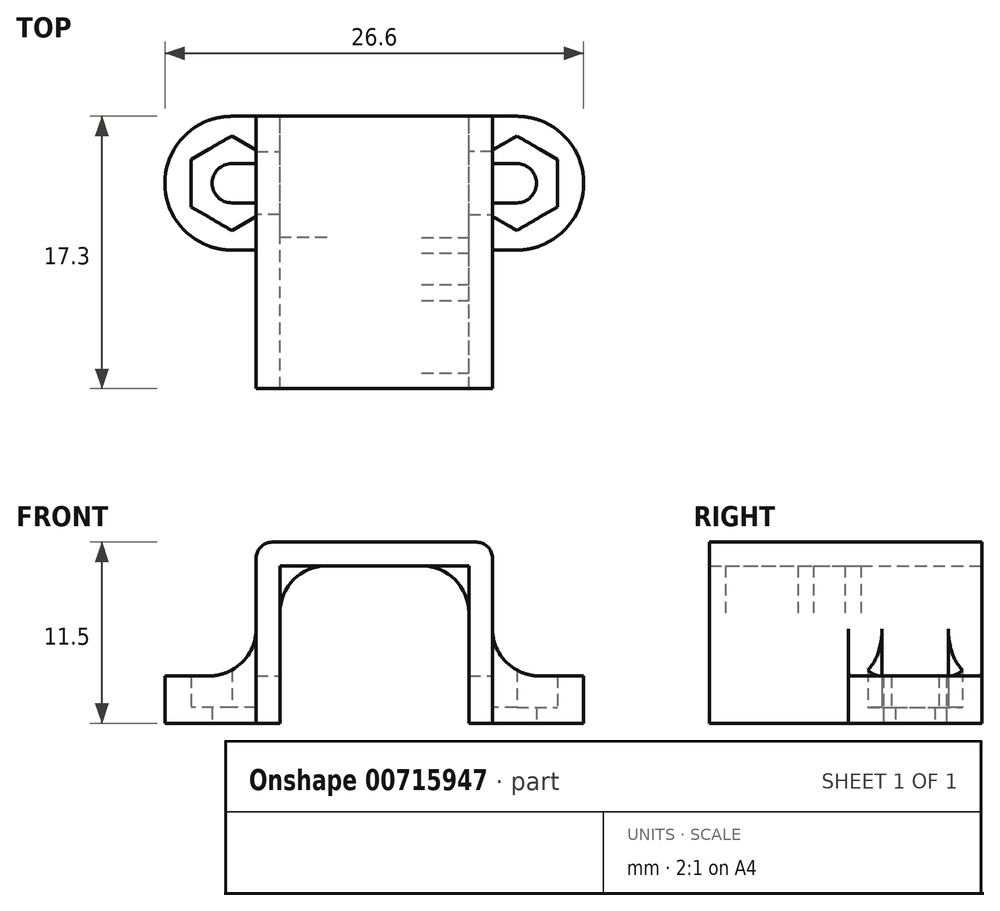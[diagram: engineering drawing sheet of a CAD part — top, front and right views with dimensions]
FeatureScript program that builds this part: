
annotation { "Feature Type Name" : "Feature", "Feature Type Description" : "" }
export const myFeature = defineFeature(function(context is Context, id is Id, definition is map)
    precondition{}
    {
        {
            var Q0;
            Q0=qCreatedBy(makeId("Front.planeOp"),FACE);
            var sketch = newSketch(context, id + "F0", { "sketchPlane" : qUnion([Q0])});
            skLineSegment(sketch, "E0", {"start": v(0, 11.5) * mm, "end": v(-6.5, 11.5) * mm});
            skLineSegment(sketch, "E1", {"start": v(-7.5, 10.5) * mm, "end": v(-7.5, 6) * mm});
            skLineSegment(sketch, "E2", {"start": v(-10.5, 3) * mm, "end": v(-13.3, 3) * mm});
            skLineSegment(sketch, "E3", {"start": v(-13.3, 3) * mm, "end": v(-13.3, 0) * mm});
            skLineSegment(sketch, "E4", {"start": v(-13.3, 0) * mm, "end": v(-6, 0) * mm});
            skLineSegment(sketch, "E5", {"start": v(-6, 0) * mm, "end": v(-6, 7) * mm});
            skLineSegment(sketch, "E6", {"start": v(-3, 10) * mm, "end": v(0, 10) * mm});
            skPoint(sketch, "E7.visualSharp", {"position": v(-7.5, 11.5) * mm});
            skArc(sketch, "E7.filletArc", {"start": v(-6.5, 11.5) * mm, "mid": v(-7.2, 11.2) * mm, "end": v(-7.5, 10.5) * mm});
            skPoint(sketch, "E8.visualSharp", {"position": v(-6, 10) * mm});
            skArc(sketch, "E8.filletArc", {"start": v(-3, 10) * mm, "mid": v(-5.12, 9.12) * mm, "end": v(-6, 7) * mm});
            skPoint(sketch, "E9.visualSharp", {"position": v(-7.5, 3) * mm});
            skArc(sketch, "E9.filletArc", {"start": v(-10.5, 3) * mm, "mid": v(-8.38, 3.88) * mm, "end": v(-7.5, 6) * mm});
            skLineSegment(sketch, "E10.MirrorCS", {"start": v(3, 10) * mm, "end": v(0, 10) * mm});
            skLineSegment(sketch, "E11.MirrorCS", {"start": v(0, 11.5) * mm, "end": v(6.5, 11.5) * mm});
            skArc(sketch, "E12.MirrorCS", {"start": v(3, 10) * mm, "mid": v(5.12, 9.12) * mm, "end": v(6, 7) * mm});
            skArc(sketch, "E13.MirrorCS", {"start": v(6.5, 11.5) * mm, "mid": v(7.2, 11.2) * mm, "end": v(7.5, 10.5) * mm});
            skLineSegment(sketch, "E14.MirrorCS", {"start": v(7.5, 10.5) * mm, "end": v(7.5, 6) * mm});
            skLineSegment(sketch, "E15.MirrorCS", {"start": v(6, 0) * mm, "end": v(6, 7) * mm});
            skArc(sketch, "E16.MirrorCS", {"start": v(10.5, 3) * mm, "mid": v(8.38, 3.88) * mm, "end": v(7.5, 6) * mm});
            skLineSegment(sketch, "E17.MirrorCS", {"start": v(10.5, 3) * mm, "end": v(13.3, 3) * mm});
            skLineSegment(sketch, "E18.MirrorCS", {"start": v(13.3, 3) * mm, "end": v(13.3, 0) * mm});
            skLineSegment(sketch, "E19.MirrorCS", {"start": v(13.3, 0) * mm, "end": v(6, 0) * mm});
            skSolve(sketch);
        }
        {
            var Q0;
            Q0=qSketchRegion(id+"F0",true);
            extrude(context, id + "F1", {"entities" : qUnion([Q0]), "depth" : 17.3 * mm});
        }
        {
            var Q0;
            Q0=makeQuery(id+"F1.opExtrude","SWEPT_FACE",FACE,{"disambiguationData":[OSD([sQuery(id+"F0.wireOp",EDGE,"E0"),sQuery(id+"F0.wireOp",EDGE,"E11.MirrorCS")])]});
            var sketch = newSketch(context, id + "F2", { "sketchPlane" : qUnion([Q0])});
            skLineSegment(sketch, "E20.2", {"start": v(-6.5, 0) * mm, "end": v(-7.5, 0) * mm});
            skLineSegment(sketch, "E20.3", {"start": v(-6.5, 0) * mm, "end": v(6.5, 0) * mm});
            skLineSegment(sketch, "E20.4", {"start": v(6.5, 0) * mm, "end": v(7.5, 0) * mm});
            skLineSegment(sketch, "E20.7", {"start": v(6.5, -17.3) * mm, "end": v(7.5, -17.3) * mm});
            skLineSegment(sketch, "E20.8", {"start": v(-6.5, -17.3) * mm, "end": v(6.5, -17.3) * mm});
            skLineSegment(sketch, "E20.9", {"start": v(-6.5, -17.3) * mm, "end": v(-7.5, -17.3) * mm});
            skLineSegment(sketch, "E21", {"start": v(-13.3, -4.25) * mm, "end": v(-13.3, -4.25) * mm});
            skLineSegment(sketch, "E22", {"start": v(-9.05, -8.5) * mm, "end": v(-7.5, -8.5) * mm});
            skLineSegment(sketch, "E23", {"start": v(-7.5, -8.5) * mm, "end": v(-7.5, -17.3) * mm});
            skLineSegment(sketch, "E24", {"start": v(7.5, -17.3) * mm, "end": v(7.5, -8.5) * mm});
            skLineSegment(sketch, "E25", {"start": v(7.5, -8.5) * mm, "end": v(9.05, -8.5) * mm});
            skLineSegment(sketch, "E26", {"start": v(13.3, -4.25) * mm, "end": v(13.3, -4.25) * mm});
            skLineSegment(sketch, "E27", {"start": v(-9.05, 0) * mm, "end": v(-7.5, 0) * mm});
            skLineSegment(sketch, "E28", {"start": v(7.5, 0) * mm, "end": v(9.05, 0) * mm});
            skPoint(sketch, "E29.visualSharp", {"position": v(-13.3, 0) * mm});
            skArc(sketch, "E29.filletArc", {"start": v(-9.05, 0) * mm, "mid": v(-12.06, -1.24) * mm, "end": v(-13.3, -4.25) * mm});
            skPoint(sketch, "E30.visualSharp", {"position": v(-13.3, -8.5) * mm});
            skArc(sketch, "E30.filletArc", {"start": v(-13.3, -4.25) * mm, "mid": v(-12.06, -7.26) * mm, "end": v(-9.05, -8.5) * mm});
            skPoint(sketch, "E31.visualSharp", {"position": v(13.3, 0) * mm});
            skArc(sketch, "E31.filletArc", {"start": v(13.3, -4.25) * mm, "mid": v(12.06, -1.24) * mm, "end": v(9.05, 0) * mm});
            skPoint(sketch, "E32.visualSharp", {"position": v(13.3, -8.5) * mm});
            skArc(sketch, "E32.filletArc", {"start": v(9.05, -8.5) * mm, "mid": v(12.06, -7.26) * mm, "end": v(13.3, -4.25) * mm});
            skSolve(sketch);
        }
        {
            var Q0;
            Q0=qSketchRegion(id+"F2",true);
            extrude(context, id + "F3", {"entities" : qUnion([Q0]), "operationType" : NewBodyOperationType.INTERSECT, "endBound" : BoundingType.THROUGH_ALL, "oppositeDirection" : true, "depth" : 25 * mm});
        }
        {
            var Q0;
            Q0=makeQuery(id+"F1.opExtrude","SWEPT_FACE",FACE,{"disambiguationData":[OSD([sQuery(id+"F0.wireOp",EDGE,"E4")])]});
            var sketch = newSketch(context, id + "F4", { "sketchPlane" : qUnion([Q0])});
            skLineSegment(sketch, "E33", {"start": v(-7.5, 5.5) * mm, "end": v(-9.05, 5.5) * mm});
            skArc(sketch, "E34", {"start": v(-9.05, 5.5) * mm, "mid": v(-10.3, 4.25) * mm, "end": v(-9.05, 3) * mm});
            skLineSegment(sketch, "E35", {"start": v(-9.05, 3) * mm, "end": v(-7.5, 3) * mm});
            skLineSegment(sketch, "E36", {"start": v(-6, 6.25) * mm, "end": v(-7.5, 6.25) * mm});
            skLineSegment(sketch, "E37", {"start": v(-7.5, 6.25) * mm, "end": v(-7.5, 5.5) * mm});
            skLineSegment(sketch, "E38", {"start": v(-7.5, 3) * mm, "end": v(-7.5, 2.25) * mm});
            skLineSegment(sketch, "E39", {"start": v(-7.5, 2.25) * mm, "end": v(-6, 2.25) * mm});
            skLineSegment(sketch, "E40", {"start": v(-6, 6.25) * mm, "end": v(-6, 2.25) * mm});
            skLineSegment(sketch, "E41", {"start": v(4.75, 4.25) * mm, "end": v(-15.15, 4.25) * mm, "construction": true});
            skPoint(sketch, "E41.endSnap0", {"position": v(-10.3, 4.25) * mm});
            skLineSegment(sketch, "E42.MirrorCS", {"start": v(6, 6.25) * mm, "end": v(7.5, 6.25) * mm});
            skLineSegment(sketch, "E43.MirrorCS", {"start": v(6, 6.25) * mm, "end": v(6, 2.25) * mm});
            skLineSegment(sketch, "E44.MirrorCS", {"start": v(7.5, 2.25) * mm, "end": v(6, 2.25) * mm});
            skLineSegment(sketch, "E45.MirrorCS", {"start": v(7.5, 3) * mm, "end": v(7.5, 2.25) * mm});
            skLineSegment(sketch, "E46.MirrorCS", {"start": v(9.05, 3) * mm, "end": v(7.5, 3) * mm});
            skLineSegment(sketch, "E47.MirrorCS", {"start": v(7.5, 5.5) * mm, "end": v(9.05, 5.5) * mm});
            skLineSegment(sketch, "E48.MirrorCS", {"start": v(7.5, 6.25) * mm, "end": v(7.5, 5.5) * mm});
            skArc(sketch, "E49.MirrorCS", {"start": v(9.05, 5.5) * mm, "mid": v(10.3, 4.25) * mm, "end": v(9.05, 3) * mm});
            skSolve(sketch);
        }
        {
            var Q0;
            Q0=qSketchRegion(id+"F4",true);
            extrude(context, id + "F5", {"entities" : qUnion([Q0]), "operationType" : NewBodyOperationType.REMOVE, "oppositeDirection" : true, "depth" : 3 * mm});
        }
        {
            var Q0;
            Q0=qCreatedBy(makeId("Top.planeOp"),FACE);
            cPlane(context, id + "F6", {"entities" : qUnion([Q0]), "cplaneType" : CPlaneType.OFFSET, "offset" : 1 * mm, "width" : 150 * mm, "height" : 150 * mm});
        }
        {
            var Q0;
            Q0=qCreatedBy(id+"F6.planeOp",FACE);
            var sketch = newSketch(context, id + "F7", { "sketchPlane" : qUnion([Q0])});
            skCircle(sketch, "E50.cCircle", {"center": v(-9.05, -4.25) * mm, "radius": 2.6 * mm, "construction": true});
            skLineSegment(sketch, "E50.0", {"start": v(-11.65, -5.75) * mm, "end": v(-11.65, -2.75) * mm});
            skLineSegment(sketch, "E50.1", {"start": v(-11.65, -2.75) * mm, "end": v(-9.05, -1.25) * mm});
            skLineSegment(sketch, "E50.2", {"start": v(-9.05, -1.25) * mm, "end": v(-7.5, -2.14) * mm});
            skLineSegment(sketch, "E50.4", {"start": v(-7.5, -6.36) * mm, "end": v(-9.05, -7.25) * mm});
            skLineSegment(sketch, "E50.5", {"start": v(-9.05, -7.25) * mm, "end": v(-11.65, -5.75) * mm});
            skPoint(sketch, "E50.0.midPoint", {"position": v(-11.65, -4.25) * mm});
            skPoint(sketch, "E51", {"position": v(-7.5, -6.36) * mm});
            skPoint(sketch, "E52", {"position": v(-7.5, -2.14) * mm});
            skLineSegment(sketch, "E53", {"start": v(-7.5, -6.36) * mm, "end": v(-7.5, -2.14) * mm});
            skLineSegment(sketch, "E54.MirrorCS", {"start": v(7.5, -6.36) * mm, "end": v(9.05, -7.25) * mm});
            skLineSegment(sketch, "E55.MirrorCS", {"start": v(9.05, -7.25) * mm, "end": v(11.65, -5.75) * mm});
            skLineSegment(sketch, "E56.MirrorCS", {"start": v(11.65, -5.75) * mm, "end": v(11.65, -2.75) * mm});
            skLineSegment(sketch, "E57.MirrorCS", {"start": v(11.65, -2.75) * mm, "end": v(9.05, -1.25) * mm});
            skLineSegment(sketch, "E58.MirrorCS", {"start": v(9.05, -1.25) * mm, "end": v(7.5, -2.14) * mm});
            skLineSegment(sketch, "E59.MirrorCS", {"start": v(7.5, -17.3) * mm, "end": v(7.5, 0) * mm, "construction": true});
            skLineSegment(sketch, "E60.MirrorCS", {"start": v(7.5, -6.36) * mm, "end": v(7.5, -2.14) * mm});
            skSolve(sketch);
        }
        {
            var Q0;
            Q0=qSketchRegion(id+"F7",true);
            extrude(context, id + "F8", {"entities" : qUnion([Q0]), "operationType" : NewBodyOperationType.REMOVE, "endBound" : BoundingType.THROUGH_ALL, "depth" : 25 * mm});
        }
        {
            var Q0;
            Q0=makeQuery(id+"F1.opExtrude","SWEPT_FACE",FACE,{"disambiguationData":[OSD([sQuery(id+"F0.wireOp",EDGE,"E19.MirrorCS")])]});
            var sketch = newSketch(context, id + "F9", { "sketchPlane" : qUnion([Q0])});
            skLineSegment(sketch, "E61.0", {"start": v(3, 17.3) * mm, "end": v(-3, 17.3) * mm, "construction": true});
            skLineSegment(sketch, "E61.1", {"start": v(-6, 17.3) * mm, "end": v(-6, 6.25) * mm, "construction": true});
            skLineSegment(sketch, "E62.bottom", {"start": v(-3, 17.3) * mm, "end": v(-6, 17.3) * mm});
            skLineSegment(sketch, "E62.top", {"start": v(-3, 7.7) * mm, "end": v(-6, 7.7) * mm});
            skLineSegment(sketch, "E62.left", {"start": v(-3, 17.3) * mm, "end": v(-3, 7.7) * mm});
            skLineSegment(sketch, "E62.right", {"start": v(-6, 17.3) * mm, "end": v(-6, 7.7) * mm});
            skLineSegment(sketch, "E63.0", {"start": v(3, 17.3) * mm, "end": v(3, 0) * mm, "construction": true});
            skLineSegment(sketch, "E63.1", {"start": v(6, 17.3) * mm, "end": v(6, 6.25) * mm, "construction": true});
            skLineSegment(sketch, "E64.bottom", {"start": v(3, 17.3) * mm, "end": v(6, 17.3) * mm});
            skLineSegment(sketch, "E64.top", {"start": v(3, 16.3) * mm, "end": v(6, 16.3) * mm});
            skLineSegment(sketch, "E64.left", {"start": v(3, 17.3) * mm, "end": v(3, 16.3) * mm});
            skLineSegment(sketch, "E64.right", {"start": v(6, 17.3) * mm, "end": v(6, 16.3) * mm});
            skLineSegment(sketch, "E65.bottom", {"start": v(3, 7.7) * mm, "end": v(6, 7.7) * mm});
            skLineSegment(sketch, "E65.top", {"start": v(3, 8.7) * mm, "end": v(6, 8.7) * mm});
            skLineSegment(sketch, "E65.left", {"start": v(3, 7.7) * mm, "end": v(3, 8.7) * mm});
            skLineSegment(sketch, "E65.right", {"start": v(6, 7.7) * mm, "end": v(6, 8.7) * mm});
            skLineSegment(sketch, "E66.bottom", {"start": v(3, 11.7) * mm, "end": v(6, 11.7) * mm});
            skLineSegment(sketch, "E66.top", {"start": v(3, 10.7) * mm, "end": v(6, 10.7) * mm});
            skLineSegment(sketch, "E66.left", {"start": v(3, 11.7) * mm, "end": v(3, 10.7) * mm});
            skLineSegment(sketch, "E66.right", {"start": v(6, 11.7) * mm, "end": v(6, 10.7) * mm});
            skSolve(sketch);
        }
        {
            var Q0;
            Q0=qSketchRegion(id+"F9",true);
            var Q1;
            Q1=makeQuery(id+"F1.opExtrude","SWEPT_FACE",FACE,{"disambiguationData":[OSD([sQuery(id+"F0.wireOp",EDGE,"E6"),sQuery(id+"F0.wireOp",EDGE,"E10.MirrorCS")])]});
            extrude(context, id + "F10", {"entities" : qUnion([Q0]), "operationType" : NewBodyOperationType.REMOVE, "endBound" : BoundingType.UP_TO_SURFACE, "oppositeDirection" : true, "endBoundEntityFace" : qUnion([Q1]), "depth" : 25 * mm});
        }
    });
